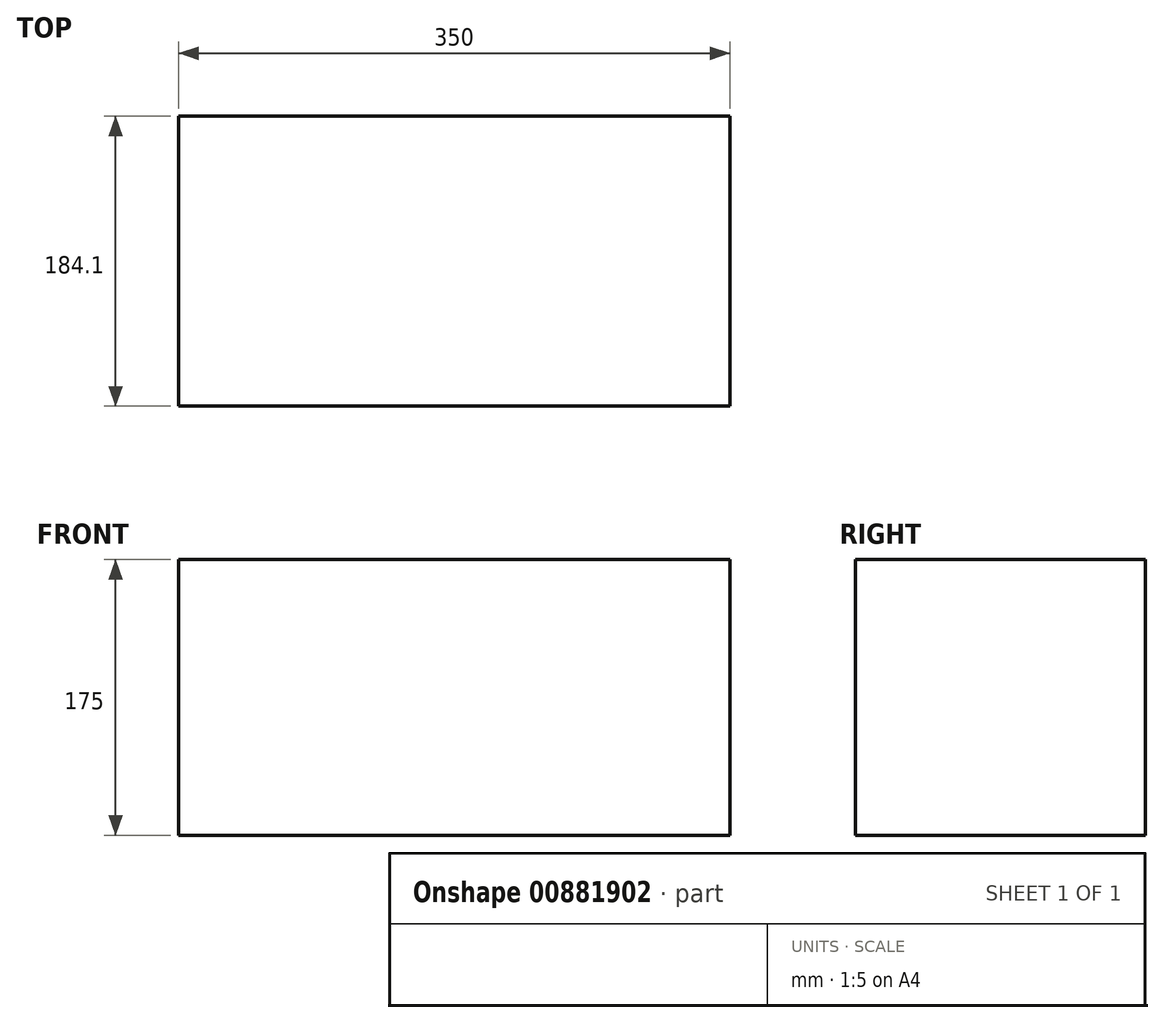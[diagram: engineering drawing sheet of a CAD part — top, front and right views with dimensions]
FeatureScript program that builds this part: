
annotation { "Feature Type Name" : "Feature", "Feature Type Description" : "" }
export const myFeature = defineFeature(function(context is Context, id is Id, definition is map)
    precondition{}
    {
        {
            var Q0;
            Q0=qCreatedBy(makeId("Top.planeOp"),FACE);
            var sketch = newSketch(context, id + "F0", { "sketchPlane" : qUnion([Q0])});
            skLineSegment(sketch, "E0.bottom", {"start": v(-175, 92.05) * mm, "end": v(175, 92.05) * mm});
            skLineSegment(sketch, "E0.top", {"start": v(-175, -92.05) * mm, "end": v(175, -92.05) * mm});
            skLineSegment(sketch, "E0.left", {"start": v(-175, 92.05) * mm, "end": v(-175, -92.05) * mm});
            skLineSegment(sketch, "E0.right", {"start": v(175, 92.05) * mm, "end": v(175, -92.05) * mm});
            skPoint(sketch, "E0.middle", {"position": v(0, 0) * mm});
            skSolve(sketch);
        }
        {
            var Q0;
            Q0 = qSketchRegion(id + "F0", true);
            extrude(context, id + "F1", {"entities" : qUnion([Q0]), "depth" : 175 * mm, "offsetDistance" : 25 * mm});
        }
    });
